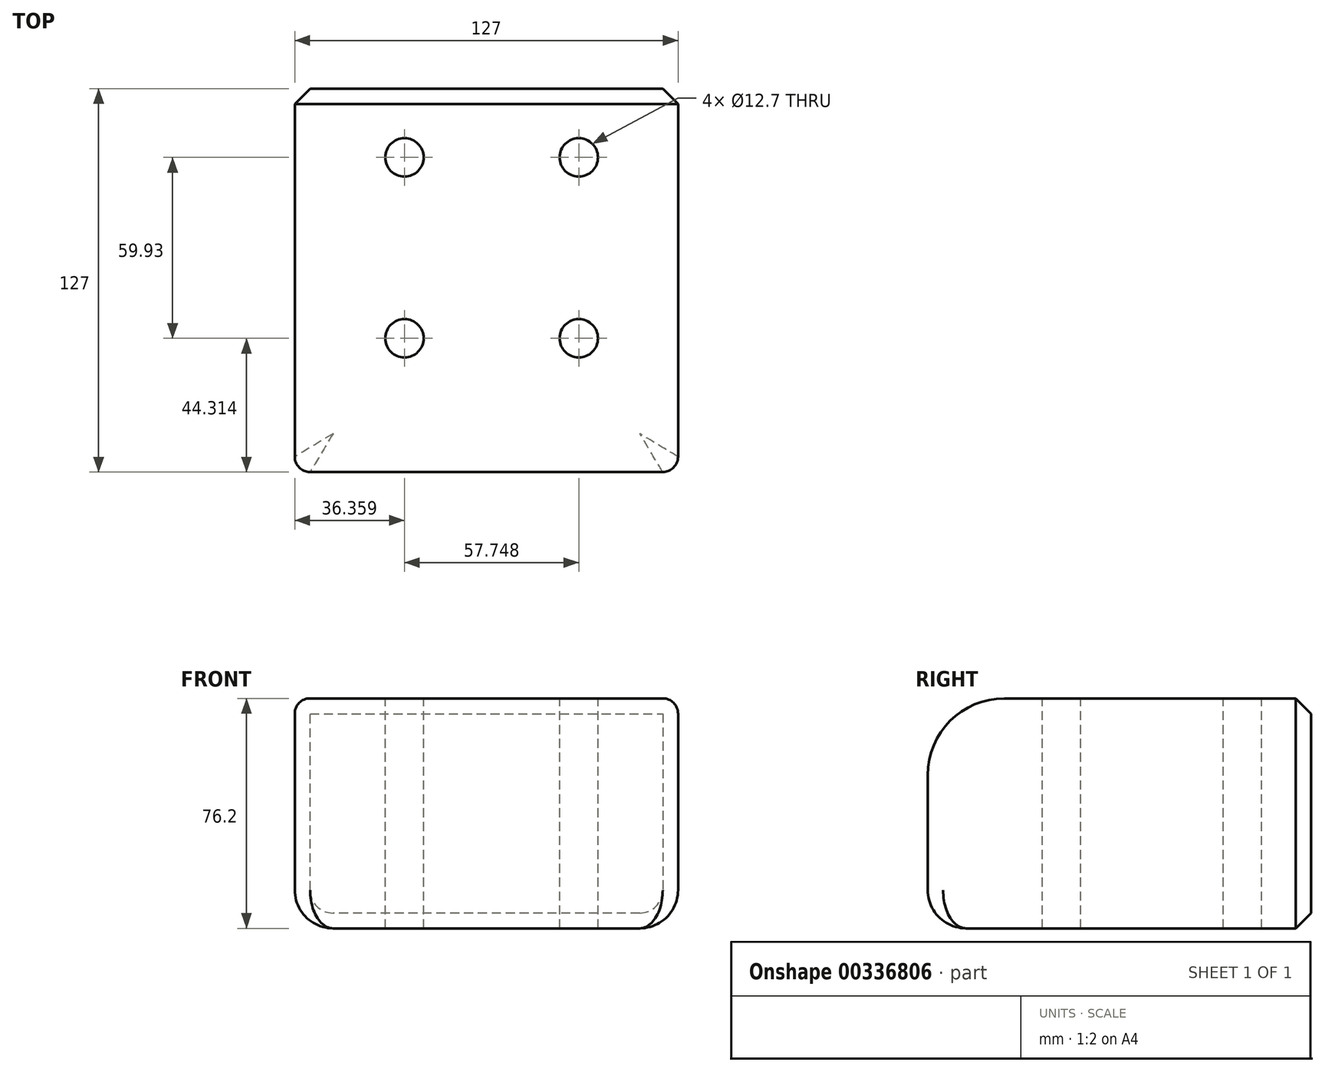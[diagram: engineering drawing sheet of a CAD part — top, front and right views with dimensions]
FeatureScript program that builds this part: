
annotation { "Feature Type Name" : "Feature", "Feature Type Description" : "" }
export const myFeature = defineFeature(function(context is Context, id is Id, definition is map)
    precondition{}
    {
        {
            var Q0;
            Q0=qCreatedBy(makeId("Front.planeOp"),FACE);
            var sketch = newSketch(context, id + "F0", { "sketchPlane" : qUnion([Q0])});
            skLineSegment(sketch, "E0.bottom", {"start": v(0, 0) * mm, "end": v(127, 0) * mm});
            skLineSegment(sketch, "E0.top", {"start": v(0, 76.2) * mm, "end": v(127, 76.2) * mm});
            skLineSegment(sketch, "E0.left", {"start": v(0, 0) * mm, "end": v(0, 76.2) * mm});
            skLineSegment(sketch, "E0.right", {"start": v(127, 0) * mm, "end": v(127, 76.2) * mm});
            skSolve(sketch);
        }
        {
            var Q0;
            Q0=makeQuery(id+"F0.imprint","IMPRINT",FACE,{"disambiguationData":[TD([[makeQuery(id+"F0.imprint","IMPRINT",EDGE,{"derivedFrom":sQuery(id+"F0.wireOp",EDGE,"E0.bottom")}),1.0]])]});
            extrude(context, id + "F1", {"entities" : qUnion([Q0]), "depth" : 127 * mm});
        }
        {
            var Q0;
            Q0=makeQuery(id+"F1.opExtrude","CAP_EDGE",EDGE,{"disambiguationData":[OSD([sQuery(id+"F0.wireOp",EDGE,"E0.top")])],"isStart":false});
            fillet(context, id + "F2", {"entities" : qUnion([Q0]), "radius" : 25.4 * mm, "tangentPropagation" : true, "allowEdgeOverflow" : false});
        }
        {
            var Q0;
            Q0=makeQuery(id+"F2.opFillet","BLEND_EDGE",EDGE,{"blendedFrom":[makeQuery(id+"F1.opExtrude","CAP_EDGE",EDGE,{"disambiguationData":[OSD([sQuery(id+"F0.wireOp",EDGE,"E0.top")])],"isStart":false}),makeQuery(id+"F1.opExtrude","SWEPT_FACE",FACE,{"disambiguationData":[OSD([sQuery(id+"F0.wireOp",EDGE,"E0.right")])]})],"blendedInto":[makeQuery(id+"F1.opExtrude","SWEPT_FACE",FACE,{"disambiguationData":[OSD([sQuery(id+"F0.wireOp",EDGE,"E0.right")])]})]});
            var Q1;
            Q1=makeQuery(id+"F1.opExtrude","SWEPT_EDGE",EDGE,{"disambiguationData":[OSD([sQuery(id+"F0.wireOp",EDGE,"E0.top"),sQuery(id+"F0.wireOp",EDGE,"E0.right")])]});
            var Q2;
            Q2=makeQuery(id+"F1.opExtrude","SWEPT_EDGE",EDGE,{"disambiguationData":[OSD([sQuery(id+"F0.wireOp",EDGE,"E0.top"),sQuery(id+"F0.wireOp",EDGE,"E0.left")])]});
            fillet(context, id + "F3", {"entities" : qUnion([Q0, Q1, Q2]), "radius" : 5.08 * mm, "tangentPropagation" : true, "allowEdgeOverflow" : false});
        }
        {
            var Q0;
            Q0=makeQuery(id+"F1.opExtrude","SWEPT_EDGE",EDGE,{"disambiguationData":[OSD([sQuery(id+"F0.wireOp",EDGE,"E0.bottom"),sQuery(id+"F0.wireOp",EDGE,"E0.left")])]});
            fillet(context, id + "F4", {"entities" : qUnion([Q0]), "radius" : 12.7 * mm, "tangentPropagation" : true, "allowEdgeOverflow" : false});
        }
        {
            var Q0;
            Q0=makeQuery(id+"F1.opExtrude","CAP_EDGE",EDGE,{"disambiguationData":[OSD([sQuery(id+"F0.wireOp",EDGE,"E0.top")])],"isStart":true});
            chamfer(context, id + "F5", {"entities" : qUnion([Q0]), "width" : 5.08 * mm, "tangentPropagation" : true});
        }
        {
            var Q0;
            Q0=makeQuery(id+"F1.opExtrude","SWEPT_FACE",FACE,{"disambiguationData":[OSD([sQuery(id+"F0.wireOp",EDGE,"E0.top")])]});
            var sketch = newSketch(context, id + "F6", { "sketchPlane" : qUnion([Q0])});
            skLineSegment(sketch, "E1.bottom", {"start": v(36.36, -22.76) * mm, "end": v(94.1, -22.76) * mm});
            skLineSegment(sketch, "E1.top", {"start": v(36.36, -82.69) * mm, "end": v(94.1, -82.69) * mm});
            skLineSegment(sketch, "E1.left", {"start": v(36.36, -22.76) * mm, "end": v(36.36, -82.69) * mm});
            skLineSegment(sketch, "E1.right", {"start": v(94.1, -22.76) * mm, "end": v(94.1, -82.69) * mm});
            skSolve(sketch);
        }
        {
            var Q0;
            Q0=sQuery(id+"F6.wireOp",VERTEX,"E1.left.start");
            var Q1;
            Q1=sQuery(id+"F6.wireOp",VERTEX,"E1.left.end");
            var Q2;
            Q2=sQuery(id+"F6.wireOp",VERTEX,"E1.top.end");
            var Q3;
            Q3=sQuery(id+"F6.wireOp",VERTEX,"E1.right.start");
            var Q4;
            Q4=makeQuery(id+"F1.opExtrude","SWEPT_BODY",BODY,{"disambiguationData":[OSD([sQuery(id+"F0.wireOp",EDGE,"E0.bottom"),sQuery(id+"F0.wireOp",EDGE,"E0.top"),sQuery(id+"F0.wireOp",EDGE,"E0.left"),sQuery(id+"F0.wireOp",EDGE,"E0.right")])]});
            hole(context, id + "F7", {"style" : HoleStyle.SIMPLE, "endStyle" : HoleEndStyle.THROUGH, "holeDiameter" : 12.7 * mm, "tappedDepth" : 12.7 * mm, "tapClearance" : 3, "locations" : qUnion([Q0, Q1, Q2, Q3]), "scope" : qUnion([Q4])});
        }
    });
